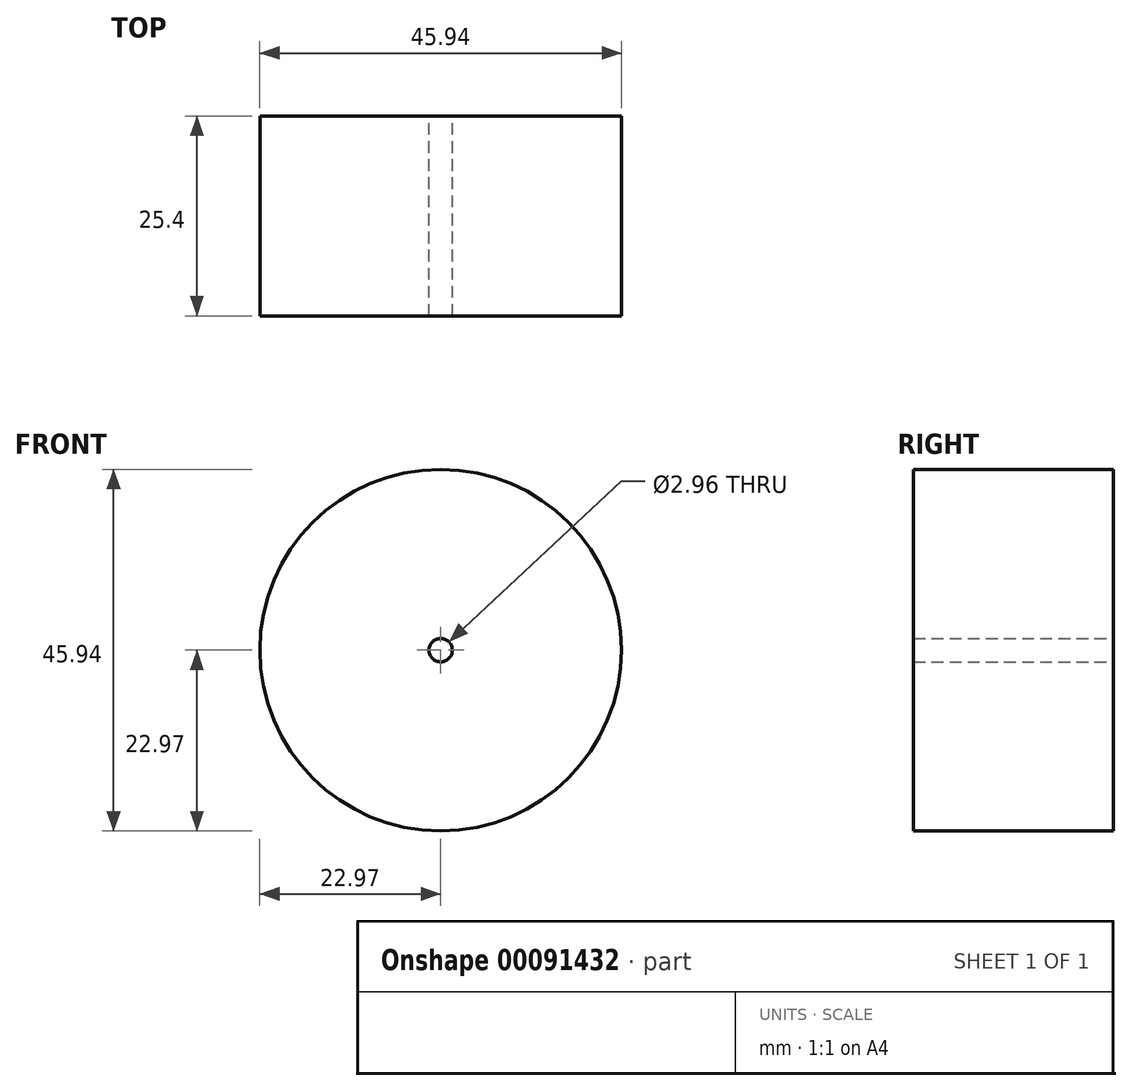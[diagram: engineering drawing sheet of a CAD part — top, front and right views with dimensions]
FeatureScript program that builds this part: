
annotation { "Feature Type Name" : "Feature", "Feature Type Description" : "" }
export const myFeature = defineFeature(function(context is Context, id is Id, definition is map)
    precondition{}
    {
        {
            var Q0;
            Q0=qCreatedBy(makeId("Front.planeOp"),FACE);
            var sketch = newSketch(context, id + "F0", { "sketchPlane" : qUnion([Q0])});
            skCircle(sketch, "E0", {"center": v(0, 0) * mm, "radius": 22.97 * mm});
            skCircle(sketch, "E1", {"center": v(0, 0) * mm, "radius": 1.48 * mm});
            skSolve(sketch);
        }
        {
            var Q0;
            Q0=makeQuery(id+"F0.imprint","IMPRINT",FACE,{"disambiguationData":[TD([[makeQuery(id+"F0.imprint","IMPRINT",EDGE,{"derivedFrom":sQuery(id+"F0.wireOp",EDGE,"E0")}),1.0]])]});
            extrude(context, id + "F1", {"entities" : qUnion([Q0]), "depth" : 25.4 * mm});
        }
    });
